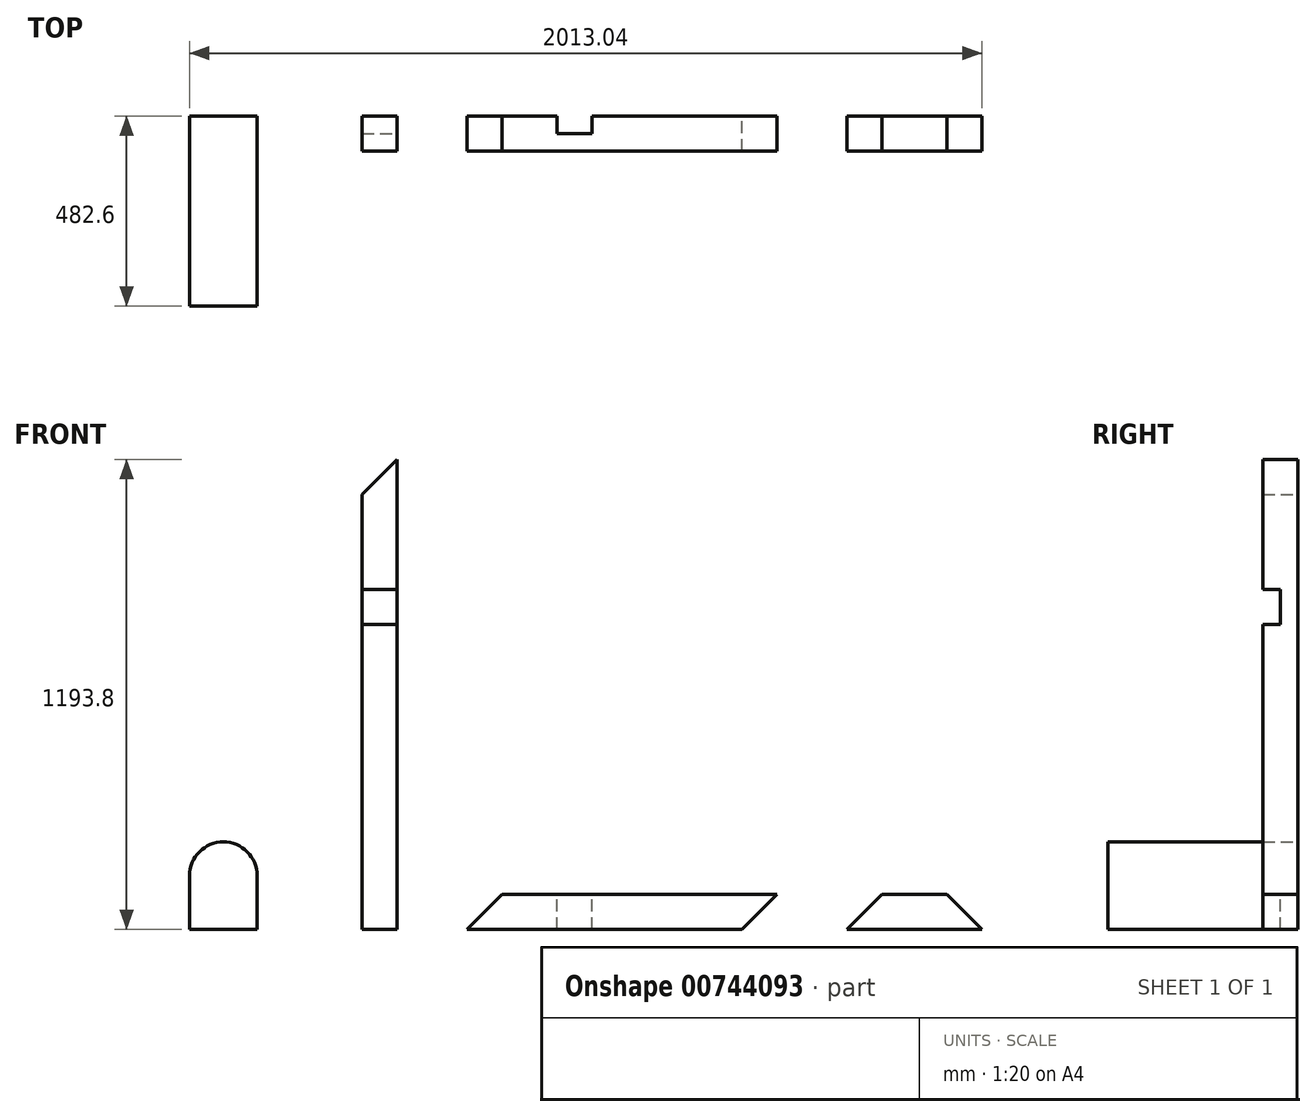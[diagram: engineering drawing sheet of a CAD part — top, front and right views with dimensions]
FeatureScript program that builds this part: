
annotation { "Feature Type Name" : "Feature", "Feature Type Description" : "" }
export const myFeature = defineFeature(function(context is Context, id is Id, definition is map)
    precondition{}
    {
        {
            var Q0;
            Q0=qCreatedBy(makeId("Front.planeOp"),FACE);
            var sketch = newSketch(context, id + "F0", { "sketchPlane" : qUnion([Q0])});
            skLineSegment(sketch, "E0", {"start": v(-781.05, 0) * mm, "end": v(-609.6, 0) * mm});
            skLineSegment(sketch, "E1", {"start": v(-781.05, 0) * mm, "end": v(-781.05, 136.53) * mm});
            skLineSegment(sketch, "E2", {"start": v(-609.6, 0) * mm, "end": v(-609.6, 136.53) * mm});
            skArc(sketch, "E3", {"start": v(-781.05, 136.53) * mm, "mid": v(-695.32, 222.25) * mm, "end": v(-609.6, 136.53) * mm});
            skSolve(sketch);
        }
        {
            var Q0;
            Q0=makeQuery(id+"F0.imprint","IMPRINT",FACE,{"disambiguationData":[TD([[makeQuery(id+"F0.imprint","IMPRINT",EDGE,{"derivedFrom":sQuery(id+"F0.wireOp",EDGE,"E0")}),1.0]])]});
            extrude(context, id + "F1", {"entities" : qUnion([Q0]), "depth" : 482.6 * mm, "offsetDistance" : 25.4 * mm});
        }
        {
            var Q0;
            Q0=qCreatedBy(makeId("Front.planeOp"),FACE);
            var sketch = newSketch(context, id + "F2", { "sketchPlane" : qUnion([Q0])});
            skLineSegment(sketch, "E4.bottom", {"start": v(-342.9, 0) * mm, "end": v(-254, 0) * mm});
            skLineSegment(sketch, "E4.left", {"start": v(-342.9, 0) * mm, "end": v(-342.9, 1104.9) * mm});
            skLineSegment(sketch, "E4.right", {"start": v(-254, 0) * mm, "end": v(-254, 1193.8) * mm});
            skLineSegment(sketch, "E5", {"start": v(-254, 1193.8) * mm, "end": v(-342.9, 1104.9) * mm});
            skSolve(sketch);
        }
        {
            var Q0;
            Q0=makeQuery(id+"F2.imprint","IMPRINT",FACE,{"disambiguationData":[TD([[makeQuery(id+"F2.imprint","IMPRINT",EDGE,{"derivedFrom":sQuery(id+"F2.wireOp",EDGE,"E4.bottom")}),1.0]])]});
            extrude(context, id + "F3", {"entities" : qUnion([Q0]), "depth" : 88.9 * mm, "offsetDistance" : 25.4 * mm});
        }
        {
            var Q0;
            Q0=makeQuery(id+"F3.opExtrude","CAP_FACE",FACE,{"disambiguationData":[OSD([sQuery(id+"F2.wireOp",EDGE,"E4.bottom"),sQuery(id+"F2.wireOp",EDGE,"E4.left"),sQuery(id+"F2.wireOp",EDGE,"E4.right"),sQuery(id+"F2.wireOp",EDGE,"E5")])],"isStart":false});
            var sketch = newSketch(context, id + "F4", { "sketchPlane" : qUnion([Q0])});
            skLineSegment(sketch, "E6.bottom", {"start": v(-342.9, 863.6) * mm, "end": v(-254, 863.6) * mm});
            skLineSegment(sketch, "E6.top", {"start": v(-342.9, 774.7) * mm, "end": v(-254, 774.7) * mm});
            skLineSegment(sketch, "E6.left", {"start": v(-342.9, 863.6) * mm, "end": v(-342.9, 774.7) * mm});
            skLineSegment(sketch, "E6.right", {"start": v(-254, 863.6) * mm, "end": v(-254, 774.7) * mm});
            skSolve(sketch);
        }
        {
            var Q0;
            Q0=makeQuery(id+"F4.imprint","IMPRINT",FACE,{"disambiguationData":[TD([[makeQuery(id+"F4.imprint","IMPRINT",EDGE,{"derivedFrom":sQuery(id+"F4.wireOp",EDGE,"E6.bottom")}),-1.0]])]});
            extrude(context, id + "F5", {"entities" : qUnion([Q0]), "operationType" : NewBodyOperationType.REMOVE, "oppositeDirection" : true, "depth" : 44.45 * mm, "offsetDistance" : 25.4 * mm});
        }
        {
            var Q0;
            Q0=qCreatedBy(makeId("Front.planeOp"),FACE);
            var sketch = newSketch(context, id + "F6", { "sketchPlane" : qUnion([Q0])});
            skLineSegment(sketch, "E7.bottom", {"start": v(-76.2, 0) * mm, "end": v(622.3, 0) * mm});
            skLineSegment(sketch, "E7.top", {"start": v(12.7, 88.9) * mm, "end": v(711.2, 88.9) * mm});
            skLineSegment(sketch, "E8", {"start": v(711.2, 88.9) * mm, "end": v(622.3, 0) * mm});
            skLineSegment(sketch, "E9", {"start": v(-76.2, 0) * mm, "end": v(12.7, 88.9) * mm});
            skSolve(sketch);
        }
        {
            var Q0;
            Q0=makeQuery(id+"F6.imprint","IMPRINT",FACE,{"disambiguationData":[TD([[makeQuery(id+"F6.imprint","IMPRINT",EDGE,{"derivedFrom":sQuery(id+"F6.wireOp",EDGE,"E7.bottom")}),1.0]])]});
            extrude(context, id + "F7", {"entities" : qUnion([Q0]), "depth" : 88.9 * mm, "offsetDistance" : 25.4 * mm});
        }
        {
            var Q0;
            Q0=makeQuery(id+"F7.opExtrude","CAP_FACE",FACE,{"disambiguationData":[OSD([sQuery(id+"F6.wireOp",EDGE,"E7.bottom"),sQuery(id+"F6.wireOp",EDGE,"E7.top"),sQuery(id+"F6.wireOp",EDGE,"E8"),sQuery(id+"F6.wireOp",EDGE,"E9")])],"isStart":true});
            var sketch = newSketch(context, id + "F8", { "sketchPlane" : qUnion([Q0])});
            skLineSegment(sketch, "E10.bottom", {"start": v(-152.4, 0) * mm, "end": v(-241.3, 0) * mm});
            skLineSegment(sketch, "E10.top", {"start": v(-152.4, 88.9) * mm, "end": v(-241.3, 88.9) * mm});
            skLineSegment(sketch, "E10.left", {"start": v(-152.4, 0) * mm, "end": v(-152.4, 88.9) * mm});
            skLineSegment(sketch, "E10.right", {"start": v(-241.3, 0) * mm, "end": v(-241.3, 88.9) * mm});
            skSolve(sketch);
        }
        {
            var Q0;
            Q0=makeQuery(id+"F8.imprint","IMPRINT",FACE,{"disambiguationData":[TD([[makeQuery(id+"F8.imprint","IMPRINT",EDGE,{"derivedFrom":sQuery(id+"F8.wireOp",EDGE,"E10.bottom")}),-1.0]])]});
            extrude(context, id + "F9", {"entities" : qUnion([Q0]), "operationType" : NewBodyOperationType.REMOVE, "oppositeDirection" : true, "depth" : 44.45 * mm, "offsetDistance" : 25.4 * mm});
        }
        {
            var Q0;
            Q0=qCreatedBy(makeId("Front.planeOp"),FACE);
            var sketch = newSketch(context, id + "F10", { "sketchPlane" : qUnion([Q0])});
            skLineSegment(sketch, "E11.bottom", {"start": v(889.1, 0) * mm, "end": v(1232, 0) * mm});
            skLineSegment(sketch, "E11.top", {"start": v(978, 88.9) * mm, "end": v(1143.1, 88.9) * mm});
            skLineSegment(sketch, "E12", {"start": v(1232, 0) * mm, "end": v(1143.1, 88.9) * mm});
            skLineSegment(sketch, "E13", {"start": v(889.1, 0) * mm, "end": v(978, 88.9) * mm});
            skSolve(sketch);
        }
        {
            var Q0;
            Q0=makeQuery(id+"F10.imprint","IMPRINT",FACE,{"disambiguationData":[TD([[makeQuery(id+"F10.imprint","IMPRINT",EDGE,{"derivedFrom":sQuery(id+"F10.wireOp",EDGE,"E11.bottom")}),1.0]])]});
            extrude(context, id + "F11", {"entities" : qUnion([Q0]), "depth" : 88.9 * mm, "offsetDistance" : 25.4 * mm});
        }
    });
